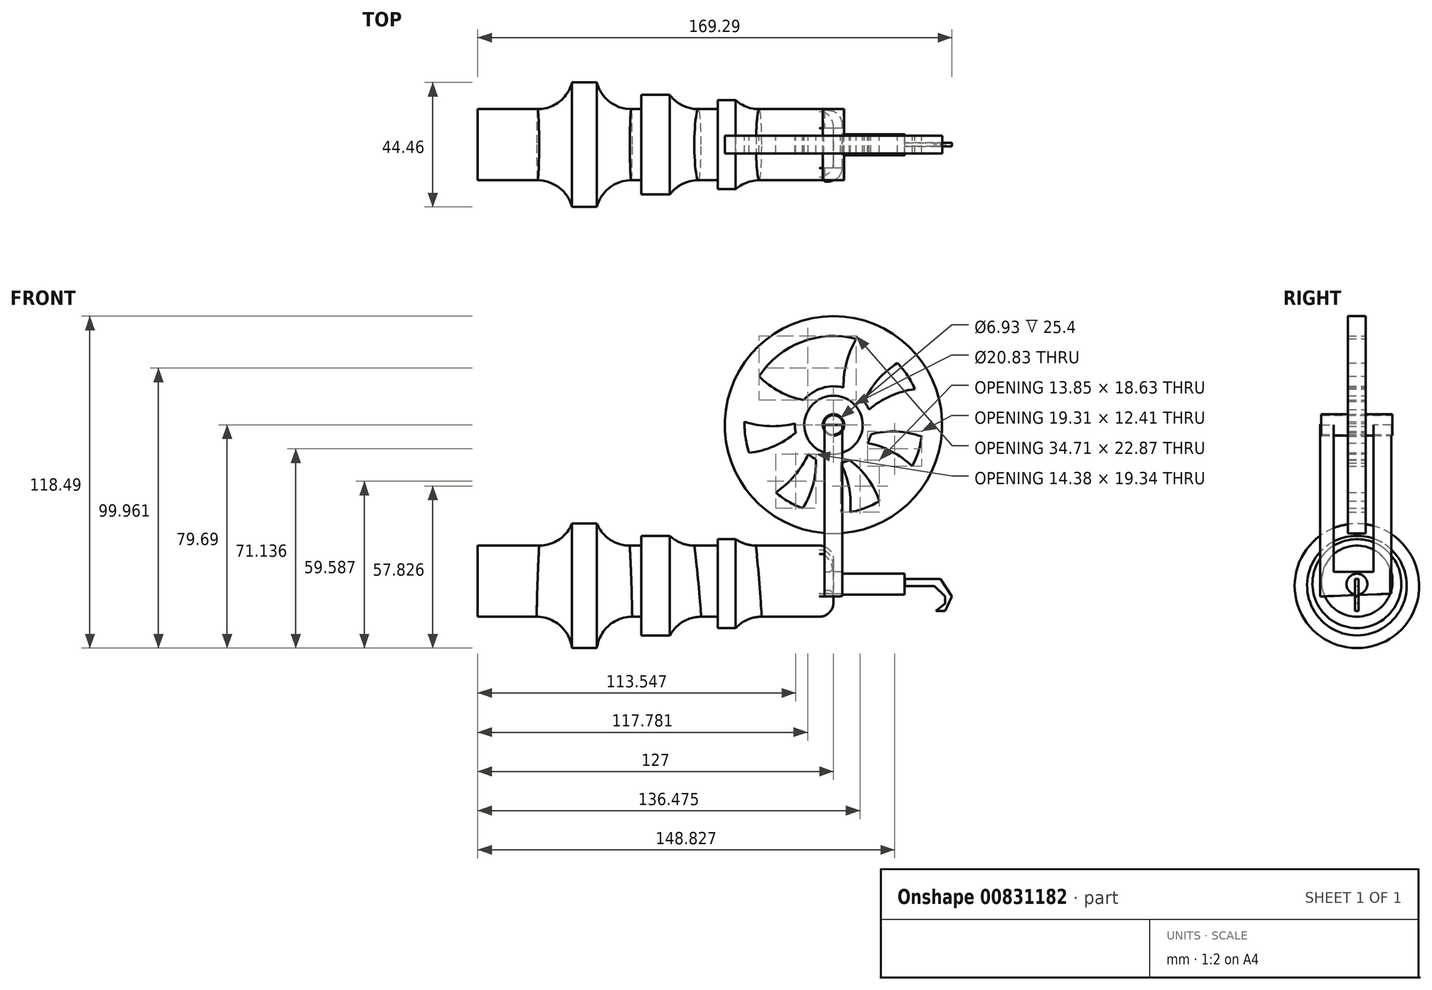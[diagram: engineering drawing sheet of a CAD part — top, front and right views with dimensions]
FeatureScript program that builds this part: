
annotation { "Feature Type Name" : "Feature", "Feature Type Description" : "" }
export const myFeature = defineFeature(function(context is Context, id is Id, definition is map)
    precondition{}
    {
        {
            var Q0;
            Q0=qCreatedBy(makeId("Front.planeOp"),FACE);
            var sketch = newSketch(context, id + "F0", { "sketchPlane" : qUnion([Q0])});
            skCircle(sketch, "E0", {"center": v(0, 0) * mm, "radius": 10.41 * mm});
            skArc(sketch, "E1", {"start": v(-1.85, 2.93) * mm, "mid": v(-2.94, 1.83) * mm, "end": v(-3.45, 0.38) * mm});
            skCircle(sketch, "E2", {"center": v(0, 0) * mm, "radius": 38.8 * mm});
            skArc(sketch, "E3", {"start": v(-5.15, 9.05) * mm, "mid": v(-5.63, 9.34) * mm, "end": v(-6.1, 9.64) * mm});
            skArc(sketch, "E4.1.1", {"start": v(3.58, 13.3) * mm, "mid": v(5.8, 25.9) * mm, "end": v(12.69, 36.67) * mm});
            skArc(sketch, "E4.2.1", {"start": v(12.63, 5.5) * mm, "mid": v(23.86, 11.61) * mm, "end": v(36.58, 12.94) * mm});
            skArc(sketch, "E4.3.1", {"start": v(12.17, -6.45) * mm, "mid": v(23.96, -11.41) * mm, "end": v(32.93, -20.53) * mm});
            skArc(sketch, "E4.4.1", {"start": v(2.55, -13.54) * mm, "mid": v(6.01, -25.85) * mm, "end": v(4.48, -38.54) * mm});
            skArc(sketch, "E4.5.1", {"start": v(-9, -10.43) * mm, "mid": v(-16.46, -20.82) * mm, "end": v(-27.34, -27.53) * mm});
            skArc(sketch, "E4.6.1", {"start": v(-10.29, 1.62) * mm, "mid": v(-10.82, 1.42) * mm, "end": v(-11.35, 1.24) * mm});
            skLineSegment(sketch, "E4.anchor1", {"start": v(0, 0) * mm, "end": v(-6.1, 9.64) * mm, "construction": true});
            skLineSegment(sketch, "E4.anchor2", {"start": v(0, 0) * mm, "end": v(-3.45, 0.38) * mm, "construction": true});
            skArc(sketch, "E5", {"start": v(0.32, 13.77) * mm, "mid": v(-3.15, 26.11) * mm, "end": v(-1.18, 38.78) * mm});
            skArc(sketch, "E6.1.0", {"start": v(-10.57, 8.84) * mm, "mid": v(-22.38, 13.82) * mm, "end": v(-31.06, 23.26) * mm});
            skArc(sketch, "E6.2.0", {"start": v(-13.5, -2.75) * mm, "mid": v(-24.76, -8.89) * mm, "end": v(-37.55, -9.79) * mm});
            skArc(sketch, "E6.3.0", {"start": v(-6.26, -12.27) * mm, "mid": v(-8.49, -24.9) * mm, "end": v(-15.76, -35.46) * mm});
            skArc(sketch, "E6.4.0", {"start": v(5.69, -12.55) * mm, "mid": v(14.17, -22.16) * mm, "end": v(17.9, -34.43) * mm});
            skArc(sketch, "E6.5.0", {"start": v(13.35, -3.38) * mm, "mid": v(26.16, -2.74) * mm, "end": v(38.08, -7.48) * mm});
            skArc(sketch, "E6.6.0", {"start": v(10.97, 8.33) * mm, "mid": v(18.45, 18.75) * mm, "end": v(29.58, 25.1) * mm});
            skCircle(sketch, "E7", {"center": v(0, 0) * mm, "radius": 31.75 * mm});
            skLineSegment(sketch, "E8.trimOffspring", {"start": v(-10.35, 1.13) * mm, "end": v(-11.35, 1.24) * mm, "construction": true});
            skCircle(sketch, "E9", {"center": v(0, 0) * mm, "radius": 13.78 * mm});
            skPoint(sketch, "E10.orphan", {"position": v(9.53, 4.2) * mm});
            skPoint(sketch, "E11.orphan", {"position": v(9.97, 3) * mm});
            skPoint(sketch, "E12.orphan", {"position": v(8.57, -5.92) * mm});
            skPoint(sketch, "E13.orphan", {"position": v(9.23, -4.82) * mm});
            skPoint(sketch, "E14.orphan", {"position": v(1.98, -10.22) * mm});
            skPoint(sketch, "E15.orphan", {"position": v(0.71, -10.39) * mm});
            skPoint(sketch, "E16.orphan", {"position": v(-6.76, -7.93) * mm});
            skPoint(sketch, "E17.orphan", {"position": v(-7.68, -7.04) * mm});
            skPoint(sketch, "E18.orphan", {"position": v(-10.4, 0.34) * mm});
            skArc(sketch, "E19.trimOffspring", {"start": v(-13.76, 0.53) * mm, "mid": v(-26.54, -0.11) * mm, "end": v(-38.57, 4.21) * mm});
            skPoint(sketch, "E20.orphan", {"position": v(-6.22, 8.35) * mm});
            skArc(sketch, "E21.trimOffspring", {"start": v(-8.17, 11.1) * mm, "mid": v(-16.63, 20.68) * mm, "end": v(-20.76, 32.78) * mm});
            skPoint(sketch, "E22.orphan", {"position": v(2.65, 10.07) * mm});
            skPoint(sketch, "E23.orphan", {"position": v(3.86, 9.67) * mm});
            skSolve(sketch);
        }
        {
            var Q0;
            Q0=qSketchRegion(id+"F0",true);
            var Q1;
            {var subQ0=sQuery(id+"F0.wireOp",EDGE,"E4.1.1");Q1=makeQuery(id+"F0.imprint","IMPRINT",FACE,{"disambiguationData":[TD([[makeQuery(id+"F0.imprint","IMPRINT",EDGE,{"derivedFrom":subQ0}),1.0]])]});}
            var Q2;
            {var subQ0=sQuery(id+"F0.wireOp",EDGE,"E4.2.1");Q2=makeQuery(id+"F0.imprint","IMPRINT",FACE,{"disambiguationData":[TD([[makeQuery(id+"F0.imprint","IMPRINT",EDGE,{"derivedFrom":subQ0}),1.0]])]});}
            var Q3;
            {var subQ0=sQuery(id+"F0.wireOp",EDGE,"E4.3.1");Q3=makeQuery(id+"F0.imprint","IMPRINT",FACE,{"disambiguationData":[TD([[makeQuery(id+"F0.imprint","IMPRINT",EDGE,{"derivedFrom":subQ0}),1.0]])]});}
            var Q4;
            {var subQ0=sQuery(id+"F0.wireOp",EDGE,"E4.4.1");Q4=makeQuery(id+"F0.imprint","IMPRINT",FACE,{"disambiguationData":[TD([[makeQuery(id+"F0.imprint","IMPRINT",EDGE,{"derivedFrom":subQ0}),1.0]])]});}
            var Q5;
            {var subQ0=sQuery(id+"F0.wireOp",EDGE,"E4.5.1");Q5=makeQuery(id+"F0.imprint","IMPRINT",FACE,{"disambiguationData":[TD([[makeQuery(id+"F0.imprint","IMPRINT",EDGE,{"derivedFrom":subQ0}),1.0]])]});}
            var Q6;
            {var subQ0=sQuery(id+"F0.wireOp",EDGE,"E6.2.0");Q6=makeQuery(id+"F0.imprint","IMPRINT",FACE,{"disambiguationData":[TD([[makeQuery(id+"F0.imprint","IMPRINT",EDGE,{"derivedFrom":subQ0}),-1.0]])]});}
            var Q7;
            {var subQ0=sQuery(id+"F0.wireOp",EDGE,"E6.1.0");Q7=makeQuery(id+"F0.imprint","IMPRINT",FACE,{"disambiguationData":[TD([[makeQuery(id+"F0.imprint","IMPRINT",EDGE,{"derivedFrom":subQ0}),-1.0]])]});}
            var Q8;
            {var subQ8=sQuery(id+"F0.wireOp",EDGE,"E0");var subQ9=makeQuery(id+"F0.imprint","IMPRINT",VERTEX,{"disambiguationData":[OD(0.0)],"derivedFrom":subQ8});Q8=makeQuery(id+"F0.imprint","IMPRINT",FACE,{"disambiguationData":[TD([[makeQuery(id+"F0.imprint","IMPRINT",EDGE,{"disambiguationData":[TD([[subQ9,-1.0]])],"derivedFrom":subQ8}),-1.0]])]});}
            var Q9;
            Q9=makeQuery(id+"F0.imprint","IMPRINT",FACE,{"disambiguationData":[TD([[makeQuery(id+"F0.imprint","IMPRINT",EDGE,{"derivedFrom":sQuery(id+"F0.wireOp",EDGE,"539e0326-62d8-41c1-9314-10fc468e663a")}),1.0]])]});
            extrude(context, id + "F1", {"entities" : qUnion([Q0, Q1, Q2, Q3, Q4, Q5, Q6, Q7, Q8, Q9]), "endBound" : BoundingType.SYMMETRIC, "depth" : 6.35 * mm, "offsetDistance" : 25.4 * mm});
        }
        {
            var Q0;
            Q0=qCreatedBy(makeId("Front.planeOp"),FACE);
            var sketch = newSketch(context, id + "F2", { "sketchPlane" : qUnion([Q0])});
            skCircle(sketch, "E24", {"center": v(0, 0) * mm, "radius": 3.47 * mm});
            skCircle(sketch, "E25", {"center": v(0, 0) * mm, "radius": 3.82 * mm});
            skSolve(sketch);
        }
        {
            var Q0;
            Q0=makeQuery(id+"F2.imprint","IMPRINT",FACE,{"disambiguationData":[TD([[makeQuery(id+"F2.imprint","IMPRINT",EDGE,{"derivedFrom":sQuery(id+"F2.wireOp",EDGE,"E24")}),-1.0]])]});
            extrude(context, id + "F3", {"entities" : qUnion([Q0]), "endBound" : BoundingType.SYMMETRIC, "depth" : 25.4 * mm, "offsetDistance" : 25.4 * mm});
        }
        {
            var Q0;
            Q0=qCreatedBy(makeId("Right.planeOp"),FACE);
            var sketch = newSketch(context, id + "F4", { "sketchPlane" : qUnion([Q0])});
            skPoint(sketch, "E26.start.orphan", {"position": v(-13.13, 0) * mm});
            skPoint(sketch, "E27.start.orphan", {"position": v(12.27, 0) * mm});
            skLineSegment(sketch, "E28", {"start": v(12.27, 0) * mm, "end": v(12.27, -60.25) * mm});
            skLineSegment(sketch, "E29", {"start": v(-13.13, 0) * mm, "end": v(-13.13, -61.26) * mm});
            skLineSegment(sketch, "E30", {"start": v(-13.13, -61.26) * mm, "end": v(12.27, -60.25) * mm});
            skLineSegment(sketch, "E31", {"start": v(-13.13, 0) * mm, "end": v(-8.3, 0) * mm});
            skLineSegment(sketch, "E32", {"start": v(-8.3, 0) * mm, "end": v(-8.3, -52.45) * mm});
            skLineSegment(sketch, "E33", {"start": v(-8.3, -52.45) * mm, "end": v(5.9, -52.45) * mm});
            skLineSegment(sketch, "E34", {"start": v(5.9, -52.45) * mm, "end": v(5.9, 0) * mm});
            skLineSegment(sketch, "E35", {"start": v(12.27, 0) * mm, "end": v(5.9, 0) * mm});
            skSolve(sketch);
        }
        {
            var Q0;
            Q0=qSketchRegion(id+"F4",true);
            extrude(context, id + "F5", {"entities" : qUnion([Q0]), "endBound" : BoundingType.SYMMETRIC, "depth" : 6.35 * mm, "offsetDistance" : 25.4 * mm});
        }
        {
            var Q0;
            Q0=qCreatedBy(makeId("Right.planeOp"),FACE);
            var sketch = newSketch(context, id + "F6", { "sketchPlane" : qUnion([Q0])});
            skCircle(sketch, "E36", {"center": v(0, -55.77) * mm, "radius": 12.7 * mm});
            skSolve(sketch);
        }
        {
            var Q0;
            Q0=qSketchRegion(id+"F6",true);
            extrude(context, id + "F7", {"entities" : qUnion([Q0]), "operationType" : NewBodyOperationType.ADD, "oppositeDirection" : true, "depth" : 127 * mm, "offsetDistance" : 25.4 * mm});
        }
        {
            var Q0;
            Q0=qCreatedBy(makeId("Right.planeOp"),FACE);
            cPlane(context, id + "F8", {"entities" : qUnion([Q0]), "cplaneType" : CPlaneType.OFFSET, "offset" : 38.1 * mm, "oppositeDirection" : true, "width" : 152.4 * mm, "height" : 152.4 * mm});
        }
        {
            var Q0;
            Q0=qCreatedBy(id+"F8.planeOp",FACE);
            var sketch = newSketch(context, id + "F9", { "sketchPlane" : qUnion([Q0])});
            skCircle(sketch, "E37", {"center": v(0, -56.66) * mm, "radius": 15.88 * mm});
            skSolve(sketch);
        }
        {
            var Q0;
            Q0=qCreatedBy(id+"F8.planeOp",FACE);
            cPlane(context, id + "F10", {"entities" : qUnion([Q0]), "cplaneType" : CPlaneType.OFFSET, "offset" : 25.4 * mm, "oppositeDirection" : true, "width" : 152.4 * mm, "height" : 152.4 * mm});
        }
        {
            var Q0;
            Q0=qCreatedBy(id+"F10.planeOp",FACE);
            var sketch = newSketch(context, id + "F11", { "sketchPlane" : qUnion([Q0])});
            skCircle(sketch, "E38", {"center": v(0, -57.35) * mm, "radius": 17.78 * mm});
            skSolve(sketch);
        }
        {
            var Q0;
            Q0=qCreatedBy(id+"F10.planeOp",FACE);
            cPlane(context, id + "F12", {"entities" : qUnion([Q0]), "cplaneType" : CPlaneType.OFFSET, "offset" : 25.4 * mm, "oppositeDirection" : true, "width" : 152.4 * mm, "height" : 152.4 * mm});
        }
        {
            var Q0;
            Q0=qCreatedBy(id+"F12.planeOp",FACE);
            var sketch = newSketch(context, id + "F13", { "sketchPlane" : qUnion([Q0])});
            skCircle(sketch, "E39", {"center": v(0, -57.47) * mm, "radius": 22.23 * mm});
            skSolve(sketch);
        }
        {
            var Q0;
            Q0=qCreatedBy(makeId("Right.planeOp"),FACE);
            var sketch = newSketch(context, id + "F14", { "sketchPlane" : qUnion([Q0])});
            skCircle(sketch, "E40", {"center": v(0, -56.85) * mm, "radius": 3.72 * mm});
            skSolve(sketch);
        }
        {
            var Q0;
            Q0=qSketchRegion(id+"F14",true);
            extrude(context, id + "F15", {"entities" : qUnion([Q0]), "operationType" : NewBodyOperationType.ADD, "depth" : 25.4 * mm, "offsetDistance" : 25.4 * mm});
        }
        {
            var Q0;
            Q0=qCreatedBy(makeId("Front.planeOp"),FACE);
            var sketch = newSketch(context, id + "F16", { "sketchPlane" : qUnion([Q0])});
            skLineSegment(sketch, "E41", {"start": v(25.48, -54.99) * mm, "end": v(38.25, -54.99) * mm});
            skLineSegment(sketch, "E42", {"start": v(38.25, -54.99) * mm, "end": v(42.29, -61.2) * mm});
            skLineSegment(sketch, "E43", {"start": v(42.29, -61.2) * mm, "end": v(39.9, -66.47) * mm});
            skLineSegment(sketch, "E44", {"start": v(39.9, -66.47) * mm, "end": v(39.9, -61.16) * mm});
            skLineSegment(sketch, "E45", {"start": v(39.9, -61.16) * mm, "end": v(36.07, -57.52) * mm});
            skLineSegment(sketch, "E46", {"start": v(36.07, -57.52) * mm, "end": v(25.46, -57.52) * mm});
            skLineSegment(sketch, "E47", {"start": v(25.46, -57.52) * mm, "end": v(25.48, -54.99) * mm});
            skSolve(sketch);
        }
        {
            var Q0;
            Q0=makeQuery(id+"F16.imprint","IMPRINT",FACE,{"disambiguationData":[TD([[makeQuery(id+"F16.imprint","IMPRINT",EDGE,{"derivedFrom":sQuery(id+"F16.wireOp",EDGE,"E41")}),-1.0]])]});
            extrude(context, id + "F17", {"entities" : qUnion([Q0]), "endBound" : BoundingType.SYMMETRIC, "depth" : 1.27 * mm, "offsetDistance" : 25.4 * mm});
        }
        {
            var Q0;
            Q0=makeQuery(id+"F13.imprint","IMPRINT",FACE,{"disambiguationData":[TD([[makeQuery(id+"F13.imprint","IMPRINT",EDGE,{"derivedFrom":sQuery(id+"F13.wireOp",EDGE,"E39")}),1.0]])]});
            extrude(context, id + "F18", {"entities" : qUnion([Q0]), "operationType" : NewBodyOperationType.ADD, "endBound" : BoundingType.SYMMETRIC, "depth" : 8.9 * mm, "offsetDistance" : 25.4 * mm});
        }
        {
            var Q0;
            Q0=makeQuery(id+"F11.imprint","IMPRINT",FACE,{"disambiguationData":[TD([[makeQuery(id+"F11.imprint","IMPRINT",EDGE,{"derivedFrom":sQuery(id+"F11.wireOp",EDGE,"E38")}),1.0]])]});
            extrude(context, id + "F19", {"entities" : qUnion([Q0]), "operationType" : NewBodyOperationType.ADD, "endBound" : BoundingType.SYMMETRIC, "depth" : 10.16 * mm, "offsetDistance" : 25.4 * mm});
        }
        {
            var Q0;
            Q0=makeQuery(id+"F9.imprint","IMPRINT",FACE,{"disambiguationData":[TD([[makeQuery(id+"F9.imprint","IMPRINT",EDGE,{"derivedFrom":sQuery(id+"F9.wireOp",EDGE,"E37")}),1.0]])]});
            extrude(context, id + "F20", {"entities" : qUnion([Q0]), "operationType" : NewBodyOperationType.ADD, "endBound" : BoundingType.SYMMETRIC, "depth" : 6.35 * mm, "offsetDistance" : 25.4 * mm});
        }
        {
            var Q0;
            {var subQ3=sQuery(id+"F4.wireOp",EDGE,"E28");var subQ4=sQuery(id+"F6.wireOp",EDGE,"E36");Q0=makeQuery(id+"F19.boolean.opBoolean","INTERSECT",EDGE,{"derivedFrom":[makeQuery(id+"F18.boolean.opBoolean","SPLIT",FACE,{"disambiguationData":[TD([makeQuery(id+"F5.opExtrude","SWEPT_FACE",FACE,{"disambiguationData":[OSD([subQ3])]})])],"derivedFrom":makeQuery(id+"F7.opExtrude","SWEPT_FACE",FACE,{"disambiguationData":[OSD([subQ4])]})}),makeQuery(id+"F19.opExtrude","CAP_FACE",FACE,{"disambiguationData":[OSD([sQuery(id+"F11.wireOp",EDGE,"E38")])],"isStart":false})]});}
            var Q1;
            {var subQ5=sQuery(id+"F4.wireOp",EDGE,"E28");var subQ7=makeQuery(id+"F5.opExtrude","SWEPT_FACE",FACE,{"disambiguationData":[OSD([subQ5])]});var subQ9=sQuery(id+"F6.wireOp",EDGE,"E36");Q1=makeQuery(id+"F20.boolean.opBoolean","INTERSECT",EDGE,{"derivedFrom":[makeQuery(id+"F19.boolean.opBoolean","SPLIT",FACE,{"disambiguationData":[TD([subQ7])],"derivedFrom":makeQuery(id+"F18.boolean.opBoolean","SPLIT",FACE,{"disambiguationData":[TD([subQ7])],"derivedFrom":makeQuery(id+"F7.opExtrude","SWEPT_FACE",FACE,{"disambiguationData":[OSD([subQ9])]})})}),makeQuery(id+"F20.opExtrude","CAP_FACE",FACE,{"disambiguationData":[OSD([sQuery(id+"F9.wireOp",EDGE,"E37")])],"isStart":false})]});}
            var Q2;
            Q2=makeQuery(id+"F18.boolean.opBoolean","INTERSECT",EDGE,{"derivedFrom":[makeQuery(id+"F7.opExtrude","SWEPT_FACE",FACE,{"disambiguationData":[OSD([sQuery(id+"F6.wireOp",EDGE,"E36")])]}),makeQuery(id+"F18.opExtrude","CAP_FACE",FACE,{"disambiguationData":[OSD([sQuery(id+"F13.wireOp",EDGE,"E39")])],"isStart":false})]});
            var Q3;
            Q3=makeQuery(id+"F18.boolean.opBoolean","INTERSECT",EDGE,{"derivedFrom":[makeQuery(id+"F7.opExtrude","SWEPT_FACE",FACE,{"disambiguationData":[OSD([sQuery(id+"F6.wireOp",EDGE,"E36")])]}),makeQuery(id+"F18.opExtrude","CAP_FACE",FACE,{"disambiguationData":[OSD([sQuery(id+"F13.wireOp",EDGE,"E39")])],"isStart":true})]});
            fillet(context, id + "F21", {"entities" : qUnion([Q0, Q1, Q2, Q3]), "radius" : 12.7 * mm, "tangentPropagation" : true, "allowEdgeOverflow" : false});
        }
        {
            var Q0;
            {var subQ0=sQuery(id+"F6.wireOp",EDGE,"E36");Q0=makeQuery(id+"F7.boolean.opBoolean","SPLIT",EDGE,{"disambiguationData":[TD([makeQuery(id+"F5.opExtrude","SWEPT_FACE",FACE,{"disambiguationData":[OSD([sQuery(id+"F4.wireOp",EDGE,"E30")])]})])],"derivedFrom":makeQuery(id+"F7.opExtrude","CAP_EDGE",EDGE,{"disambiguationData":[OSD([subQ0])],"isStart":true})});}
            var Q1;
            {var subQ0=sQuery(id+"F6.wireOp",EDGE,"E36");Q1=makeQuery(id+"F7.boolean.opBoolean","SPLIT",EDGE,{"disambiguationData":[TD([makeQuery(id+"F5.opExtrude","SWEPT_FACE",FACE,{"disambiguationData":[OSD([sQuery(id+"F4.wireOp",EDGE,"E32")])]})])],"derivedFrom":makeQuery(id+"F7.opExtrude","CAP_EDGE",EDGE,{"disambiguationData":[OSD([subQ0])],"isStart":true})});}
            var Q2;
            Q2=makeQuery(id+"F5.opExtrude","CAP_EDGE",EDGE,{"disambiguationData":[OSD([sQuery(id+"F4.wireOp",EDGE,"E28")])],"isStart":false});
            var Q3;
            Q3=makeQuery(id+"F5.opExtrude","CAP_EDGE",EDGE,{"disambiguationData":[OSD([sQuery(id+"F4.wireOp",EDGE,"E29")])],"isStart":false});
            fillet(context, id + "F22", {"entities" : qUnion([Q0, Q1, Q2, Q3]), "radius" : 5.08 * mm, "tangentPropagation" : true, "allowEdgeOverflow" : false});
        }
        {
            var Q0;
            Q0=makeQuery(id+"F17.opExtrude","CAP_FACE",FACE,{"disambiguationData":[OSD([sQuery(id+"F16.wireOp",EDGE,"E41"),sQuery(id+"F16.wireOp",EDGE,"E42"),sQuery(id+"F16.wireOp",EDGE,"E43"),sQuery(id+"F16.wireOp",EDGE,"E44"),sQuery(id+"F16.wireOp",EDGE,"E45"),sQuery(id+"F16.wireOp",EDGE,"E46"),sQuery(id+"F16.wireOp",EDGE,"E47")])],"isStart":false});
            var sketch = newSketch(context, id + "F23", { "sketchPlane" : qUnion([Q0])});
            skLineSegment(sketch, "E48", {"start": v(39.9, -66.47) * mm, "end": v(36.53, -66.47) * mm});
            skLineSegment(sketch, "E49", {"start": v(36.53, -66.47) * mm, "end": v(39.9, -63.81) * mm});
            skSolve(sketch);
        }
        {
            var Q0;
            {var subQ0=sQuery(id+"F23.wireOp",EDGE,"E48");Q0=makeQuery(id+"F23.imprint","IMPRINT",FACE,{"disambiguationData":[TD([[makeQuery(id+"F23.imprint","IMPRINT",EDGE,{"derivedFrom":subQ0}),-1.0]])]});}
            var sketch = newSketch(context, id + "F24", { "sketchPlane" : qUnion([Q0])});
            skSolve(sketch);
        }
        {
            var Q0;
            {var subQ0=sQuery(id+"F23.wireOp",EDGE,"E48");Q0=makeQuery(id+"F24.imprint","IMPRINT",FACE,{"disambiguationData":[TD([[makeQuery(id+"F24.imprint","IMPRINT",EDGE,{"derivedFrom":makeQuery(id+"F23.imprint","IMPRINT",EDGE,{"derivedFrom":subQ0})}),-1.0]])]});}
            extrude(context, id + "F25", {"entities" : qUnion([Q0]), "operationType" : NewBodyOperationType.ADD, "oppositeDirection" : true, "depth" : 1.27 * mm, "offsetDistance" : 25.4 * mm});
        }
    });
